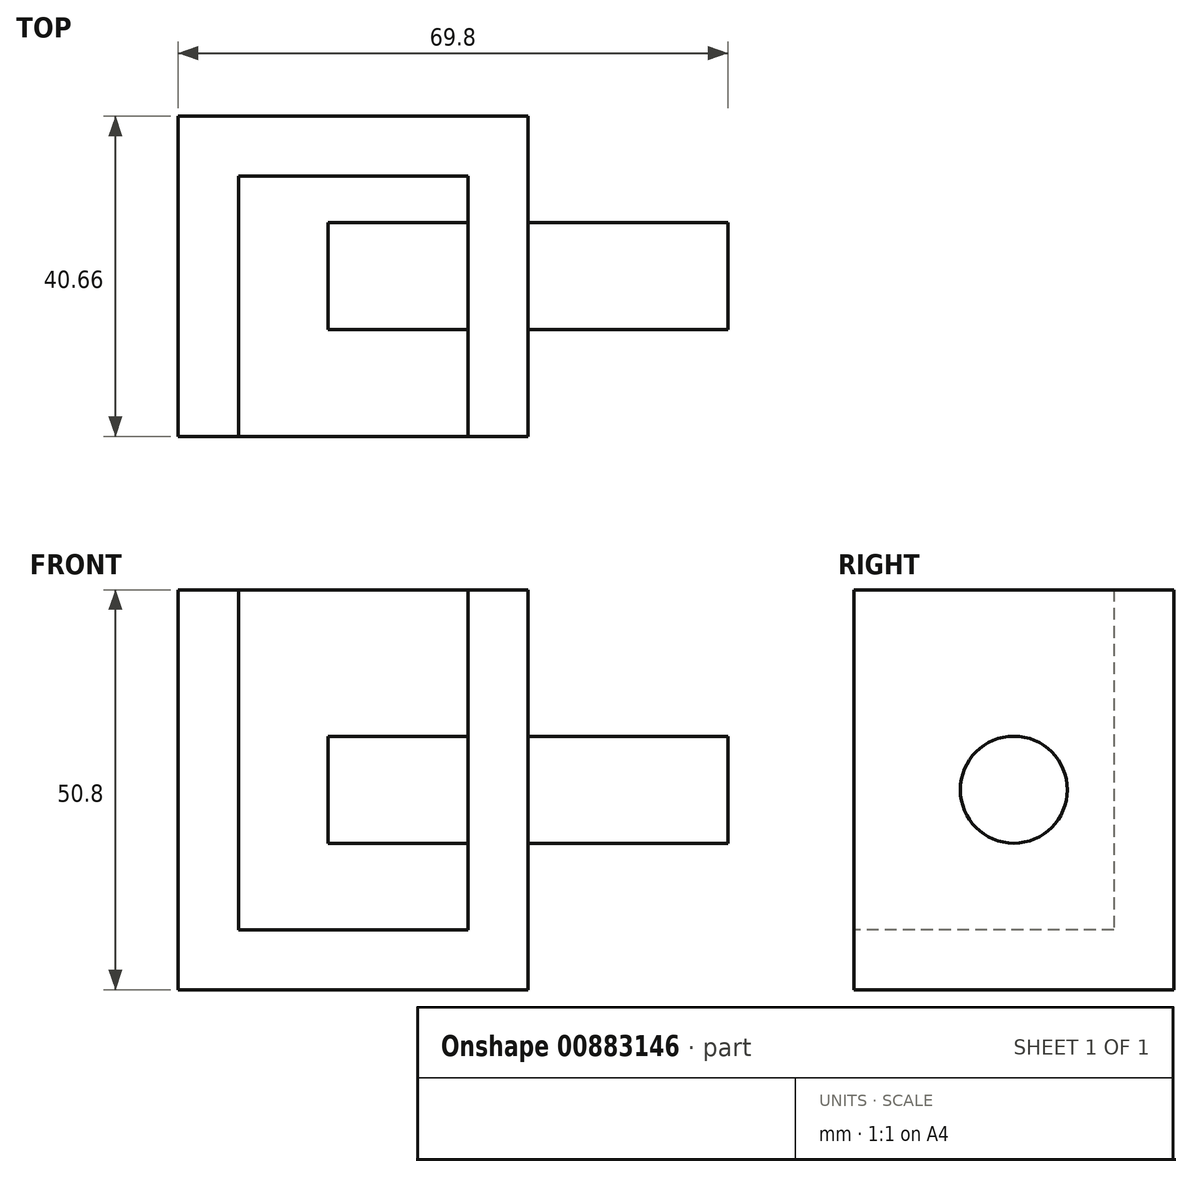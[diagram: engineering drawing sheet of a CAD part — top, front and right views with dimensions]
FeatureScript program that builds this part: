
annotation { "Feature Type Name" : "Feature", "Feature Type Description" : "" }
export const myFeature = defineFeature(function(context is Context, id is Id, definition is map)
    precondition{}
    {
        {
            var Q0;
            Q0=qCreatedBy(makeId("Top.planeOp"),FACE);
            var sketch = newSketch(context, id + "F0", { "sketchPlane" : qUnion([Q0])});
            skLineSegment(sketch, "E0.bottom", {"start": v(22.2, 20.33) * mm, "end": v(-22.2, 20.33) * mm});
            skLineSegment(sketch, "E0.top", {"start": v(22.2, -20.33) * mm, "end": v(-22.2, -20.33) * mm});
            skLineSegment(sketch, "E0.left", {"start": v(22.2, 20.33) * mm, "end": v(22.2, -20.33) * mm});
            skLineSegment(sketch, "E0.right", {"start": v(-22.2, 20.33) * mm, "end": v(-22.2, -20.33) * mm});
            skPoint(sketch, "E0.middle", {"position": v(0, 0) * mm});
            skSolve(sketch);
        }
        {
            var Q0;
            Q0=makeQuery(id+"F0.imprint","IMPRINT",FACE,{"disambiguationData":[TD([[makeQuery(id+"F0.imprint","IMPRINT",EDGE,{"derivedFrom":sQuery(id+"F0.wireOp",EDGE,"E0.bottom")}),1.0]])]});
            extrude(context, id + "F1", {"entities" : qUnion([Q0]), "depth" : 25.4 * mm, "offsetDistance" : 25.4 * mm});
        }
        {
            var Q0;
            Q0=makeQuery(id+"F1.opExtrude","CAP_FACE",FACE,{"disambiguationData":[OSD([sQuery(id+"F0.wireOp",EDGE,"E0.bottom"),sQuery(id+"F0.wireOp",EDGE,"E0.top"),sQuery(id+"F0.wireOp",EDGE,"E0.left"),sQuery(id+"F0.wireOp",EDGE,"E0.right")])],"isStart":true});
            extrude(context, id + "F2", {"entities" : qUnion([Q0]), "operationType" : NewBodyOperationType.ADD, "depth" : 25.4 * mm, "offsetDistance" : 25.4 * mm});
        }
        {
            var Q0;
            {var subQ0=sQuery(id+"F0.wireOp",EDGE,"E0.top");Q0=makeQuery(id+"F2.boolean.opBoolean","MERGE",FACE,{"derivedFrom":[makeQuery(id+"F1.opExtrude","SWEPT_FACE",FACE,{"disambiguationData":[OSD([subQ0])]}),makeQuery(id+"F2.opExtrude","SWEPT_FACE",FACE,{"disambiguationData":[OSD([subQ0])]})]});}
            var Q1;
            Q1=makeQuery(id+"F1.opExtrude","CAP_FACE",FACE,{"disambiguationData":[OSD([sQuery(id+"F0.wireOp",EDGE,"E0.bottom"),sQuery(id+"F0.wireOp",EDGE,"E0.top"),sQuery(id+"F0.wireOp",EDGE,"E0.left"),sQuery(id+"F0.wireOp",EDGE,"E0.right")])],"isStart":false});
            shell(context, id + "F3", {"entities" : qUnion([Q0, Q1]), "thickness" : 7.62 * mm});
        }
        {
            var Q0;
            {var subQ0=sQuery(id+"F0.wireOp",EDGE,"E0.left");Q0=makeQuery(id+"F2.boolean.opBoolean","MERGE",FACE,{"derivedFrom":[makeQuery(id+"F1.opExtrude","SWEPT_FACE",FACE,{"disambiguationData":[OSD([subQ0])]}),makeQuery(id+"F2.opExtrude","SWEPT_FACE",FACE,{"disambiguationData":[OSD([subQ0])]})]});}
            var sketch = newSketch(context, id + "F4", { "sketchPlane" : qUnion([Q0])});
            skCircle(sketch, "E1", {"center": v(0, 0) * mm, "radius": 6.8 * mm});
            skSolve(sketch);
        }
        {
            var Q0;
            Q0=makeQuery(id+"F4.imprint","IMPRINT",FACE,{"disambiguationData":[TD([[makeQuery(id+"F4.imprint","IMPRINT",EDGE,{"derivedFrom":sQuery(id+"F4.wireOp",EDGE,"E1")}),1.0]])]});
            extrude(context, id + "F5", {"entities" : qUnion([Q0]), "operationType" : NewBodyOperationType.ADD, "oppositeDirection" : true, "depth" : 25.4 * mm, "offsetDistance" : 25.4 * mm});
        }
        {
            var Q0;
            Q0=makeQuery(id+"F5.opExtrude","CAP_FACE",FACE,{"disambiguationData":[OSD([sQuery(id+"F4.wireOp",EDGE,"E1")])],"isStart":false});
            extrude(context, id + "F6", {"entities" : qUnion([Q0]), "operationType" : NewBodyOperationType.ADD, "oppositeDirection" : true, "depth" : 50.8 * mm, "offsetDistance" : 25.4 * mm});
        }
    });
